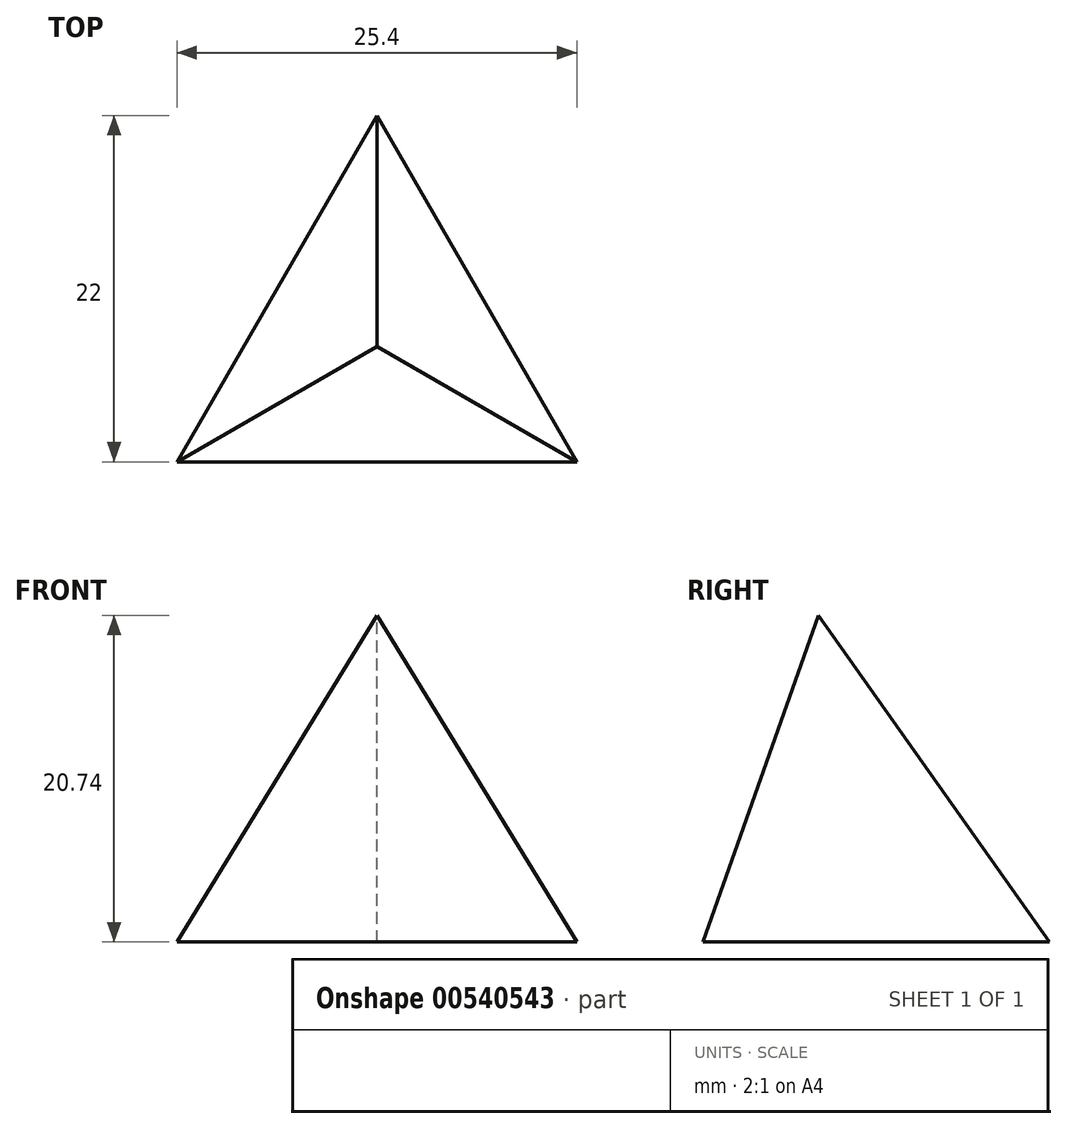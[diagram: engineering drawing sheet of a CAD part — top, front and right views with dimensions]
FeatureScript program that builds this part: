
annotation { "Feature Type Name" : "Feature", "Feature Type Description" : "" }
export const myFeature = defineFeature(function(context is Context, id is Id, definition is map)
    precondition{}
    {
        {
            var Q0;
            Q0=qCreatedBy(makeId("Top.planeOp"),FACE);
            var sketch = newSketch(context, id + "F0", { "sketchPlane" : qUnion([Q0])});
            skLineSegment(sketch, "E0", {"start": v(0, 22) * mm, "end": v(-12.7, 0) * mm});
            skLineSegment(sketch, "E1", {"start": v(-12.7, 0) * mm, "end": v(12.7, 0) * mm});
            skLineSegment(sketch, "E2", {"start": v(12.7, 0) * mm, "end": v(0, 22) * mm});
            skSolve(sketch);
        }
        {
            var Q0;
            Q0=qCreatedBy(makeId("Top.planeOp"),FACE);
            cPlane(context, id + "F1", {"entities" : qUnion([Q0]), "cplaneType" : CPlaneType.OFFSET, "offset" : 20.74 * mm, "width" : 152.4 * mm, "height" : 152.4 * mm});
        }
        {
            var Q0;
            Q0=qCreatedBy(id+"F1.planeOp",FACE);
            var sketch = newSketch(context, id + "F2", { "sketchPlane" : qUnion([Q0])});
            skPoint(sketch, "E3", {"position": v(0, 7.33) * mm});
            skLineSegment(sketch, "E4", {"start": v(-12.7, 0) * mm, "end": v(12.7, 0) * mm});
            skPoint(sketch, "E5", {"position": v(0, 0) * mm});
            skLineSegment(sketch, "E6", {"start": v(-12.7, 0) * mm, "end": v(0, 22) * mm});
            skLineSegment(sketch, "E7", {"start": v(0, 22) * mm, "end": v(12.7, 0) * mm});
            skLineSegment(sketch, "E8", {"start": v(0, 7.33) * mm, "end": v(-6.35, 11) * mm});
            skLineSegment(sketch, "E9", {"start": v(0, 7.33) * mm, "end": v(6.35, 11) * mm});
            skLineSegment(sketch, "E10", {"start": v(0, 7.33) * mm, "end": v(0, 0) * mm});
            skSolve(sketch);
        }
        {
            var Q0;
            Q0=makeQuery(id+"F0.imprint","IMPRINT",FACE,{"disambiguationData":[TD([[makeQuery(id+"F0.imprint","IMPRINT",EDGE,{"derivedFrom":sQuery(id+"F0.wireOp",EDGE,"E0")}),1.0]])]});
            var Q1;
            Q1=sQuery(id+"F2.wireOp",VERTEX,"E3");
            loft(context, id + "F3", {"sheetProfilesArray" : [{ "sheetProfileEntities" : qUnion([Q0]) }, { "sheetProfileEntities" : qUnion([Q1]) }]});
        }
    });
